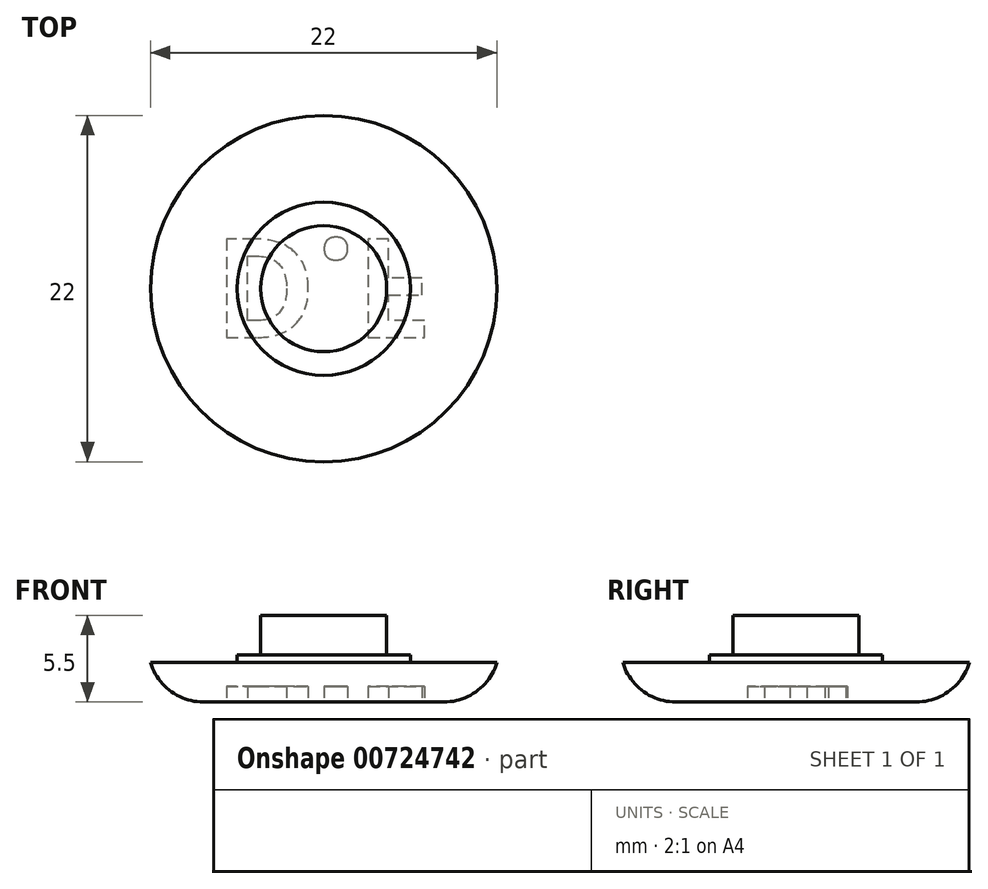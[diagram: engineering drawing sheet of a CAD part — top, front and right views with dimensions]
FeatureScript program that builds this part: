
annotation { "Feature Type Name" : "Feature", "Feature Type Description" : "" }
export const myFeature = defineFeature(function(context is Context, id is Id, definition is map)
    precondition{}
    {
        {
            var Q0;
            Q0=qCreatedBy(makeId("Top.planeOp"),FACE);
            var sketch = newSketch(context, id + "F0", { "sketchPlane" : qUnion([Q0])});
            skCircle(sketch, "E0", {"center": v(0, 0) * mm, "radius": 11 * mm});
            skCircle(sketch, "E1", {"center": v(0, 0) * mm, "radius": 4 * mm});
            skCircle(sketch, "E2", {"center": v(0, 0) * mm, "radius": 5.5 * mm});
            skSolve(sketch);
        }
        {
            var Q0;
            Q0=makeQuery(id+"F0.imprint","IMPRINT",FACE,{"disambiguationData":[TD([[makeQuery(id+"F0.imprint","IMPRINT",EDGE,{"derivedFrom":sQuery(id+"F0.wireOp",EDGE,"E0")}),1.0]])]});
            extrude(context, id + "F1", {"entities" : qUnion([Q0]), "depth" : 2.5 * mm, "offsetDistance" : 25 * mm});
        }
        {
            var Q0;
            Q0=makeQuery(id+"F0.imprint","IMPRINT",FACE,{"disambiguationData":[TD([[makeQuery(id+"F0.imprint","IMPRINT",EDGE,{"derivedFrom":sQuery(id+"F0.wireOp",EDGE,"E1")}),-1.0]])]});
            var Q1;
            Q1=makeQuery(id+"F1.opExtrude","CAP_FACE",FACE,{"disambiguationData":[OSD([sQuery(id+"F0.wireOp",EDGE,"E0"),sQuery(id+"F0.wireOp",EDGE,"E2")])],"isStart":false});
            extrude(context, id + "F2", {"entities" : qUnion([Q0]), "operationType" : NewBodyOperationType.ADD, "endBound" : BoundingType.UP_TO_SURFACE, "depth" : 25 * mm, "endBoundEntityFace" : qUnion([Q1]), "hasOffset" : true, "offsetDistance" : .5 * mm, "offsetOppositeDirection" : true});
        }
        {
            var Q0;
            Q0=makeQuery(id+"F0.imprint","IMPRINT",FACE,{"disambiguationData":[TD([[makeQuery(id+"F0.imprint","IMPRINT",EDGE,{"derivedFrom":sQuery(id+"F0.wireOp",EDGE,"E1")}),1.0]])]});
            var Q1;
            Q1=makeQuery(id+"F2.opExtrude","CAP_FACE",FACE,{"disambiguationData":[OSD([sQuery(id+"F0.wireOp",EDGE,"E0"),sQuery(id+"F0.wireOp",EDGE,"E2")])],"isStart":false});
            extrude(context, id + "F3", {"entities" : qUnion([Q0]), "operationType" : NewBodyOperationType.ADD, "endBound" : BoundingType.UP_TO_SURFACE, "depth" : 3 * mm, "endBoundEntityFace" : qUnion([Q1]), "hasOffset" : true, "offsetDistance" : 2.5 * mm, "offsetOppositeDirection" : true});
        }
        {
            var Q0;
            {var subQ0=sQuery(id+"F0.wireOp",EDGE,"E1");var subQ1=sQuery(id+"F0.wireOp",EDGE,"E2");Q0=makeQuery(id+"F3.boolean.opBoolean","MERGE",FACE,{"derivedFrom":[makeQuery(id+"F2.boolean.opBoolean","MERGE",FACE,{"derivedFrom":[makeQuery(id+"F1.opExtrude","CAP_FACE",FACE,{"disambiguationData":[OSD([sQuery(id+"F0.wireOp",EDGE,"E0"),subQ1])],"isStart":true}),makeQuery(id+"F2.opExtrude","CAP_FACE",FACE,{"disambiguationData":[OSD([subQ0,subQ1])],"isStart":true})]}),makeQuery(id+"F3.opExtrude","CAP_FACE",FACE,{"disambiguationData":[OSD([subQ0])],"isStart":true})]});}
            fillet(context, id + "F4", {"entities" : qUnion([Q0]), "radius" : 3.5 * mm, "tangentPropagation" : true, "allowEdgeOverflow" : false});
        }
        {
            var Q0;
            Q0=qCreatedBy(makeId("Right.planeOp"),FACE);
            var sketch = newSketch(context, id + "F5", { "sketchPlane" : qUnion([Q0])});
            skEllipse(sketch, "E3", {"center": v(-63.43, -1.89) * mm, "majorRadius": 11 * mm, "minorRadius": 2.5 * mm, "majorAxis": v(-1, 0)});
            skPoint(sketch, "E4", {"position": v(-63.43, 0.61) * mm});
            skLineSegment(sketch, "E5", {"start": v(-55.79, 0) * mm, "end": v(-71.08, 0) * mm});
            skArc(sketch, "E6", {"start": v(4.15, 3.3) * mm, "mid": v(11.14, 3.63) * mm, "end": v(4.15, 3.44) * mm});
            skArc(sketch, "E7", {"start": v(-11.15, 3.45) * mm, "mid": v(-11.14, 3.38) * mm, "end": v(-11.14, 3.3) * mm});
            skLineSegment(sketch, "E8", {"start": v(-63.43, 0.61) * mm, "end": v(-63.43, -4.39) * mm});
            skPoint(sketch, "E9.orphan", {"position": v(-63.43, -3.78) * mm});
            skPoint(sketch, "E10.orphan", {"position": v(-63.43, 0) * mm});
            skSolve(sketch);
        }
        {
            var Q0;
            {var subQ0=sQuery(id+"F0.wireOp",EDGE,"E1");var subQ1=sQuery(id+"F0.wireOp",EDGE,"E2");Q0=makeQuery(id+"F3.boolean.opBoolean","MERGE",FACE,{"derivedFrom":[makeQuery(id+"F2.boolean.opBoolean","MERGE",FACE,{"derivedFrom":[makeQuery(id+"F1.opExtrude","CAP_FACE",FACE,{"disambiguationData":[OSD([sQuery(id+"F0.wireOp",EDGE,"E0"),subQ1])],"isStart":true}),makeQuery(id+"F2.opExtrude","CAP_FACE",FACE,{"disambiguationData":[OSD([subQ0,subQ1])],"isStart":true})]}),makeQuery(id+"F3.opExtrude","CAP_FACE",FACE,{"disambiguationData":[OSD([subQ0])],"isStart":true})]});}
            var sketch = newSketch(context, id + "F6", { "sketchPlane" : qUnion([Q0])});
            skText(sketch, "E11", { "text": "D.F", "fontName": "OpenSans-Bold.ttf"});
            const initialGuessF6  = {"E11": [-0.00696, -0.00316, 1, 0, 0.00631]};
            skSetInitialGuess(sketch, initialGuessF6);
            skSolve(sketch);
        }
        {
            var Q0;
            Q0=qSketchRegion(id+"F6",true);
            extrude(context, id + "F7", {"entities" : qUnion([Q0]), "operationType" : NewBodyOperationType.REMOVE, "oppositeDirection" : true, "depth" : 1 * mm, "offsetDistance" : 25 * mm});
        }
    });
